# Revit family: JC KONTAKTER JCK119 Armbågskontakt
name_source: partatom
category: Specialty Equipment
units: mm (PartAtom-declared; Revit-internal decimal feet)

## family parameters
Always vertical = Yes
Cut with Voids When Loaded = No
Enable Cutting in Views = Yes
Host = Wall
Maintain Annotation Orientation = No
Part Type = Normal
Room Calculation Point = No
Round Connector Dimension = Use Diameter
Shared = No

## types (1)
- Armbågskontakt JCK119
    Antal mikrobrytare = 1
    CE Dokument = https://jckontakter.se
    Core Finish = Aluminum ENAW 6060 (guldeoxerad)
    Default Elevation = 0 mm  [stored 0 ft]
    Description = JCK119 är en tålig armbågskontakt med plan tryckplatta och endcap i mässing, samt underdel i guldeloxerad aluminium. Modellen är utvecklad för att användas i exklusiva miljöer och i äldre, k-märkta byggnader. JCK119 går bra att beställa med radiostyrning då det ofta är svårt att komma fram med kablage i äldre byggnader.
    End Cap Finish = Mässing
    Lid Finish = Mässing
    Längsta märkström = 1mA/4 V DC
    Manufacturer = JC Kontakter
    Microbrytare = Standard NO IP67
    Model = JCK119
    Nominell märkström = 12 V - Resistive 6A Inductive L/R 5ms 6A, 24 V - Resistive 6A Inductive L/R 5ms 5A
    Placering information = https://jckontakter.se
    Produktvikt = 0.579 kg
    Screw Finish = Mässing
    Teknisk produktblad = https://jckontakter.se
    Tillvalsförteckning = https://jckontakter.se
    Tillverkarens land = Sverige
    URL = https://jckontakter.se

note: [stored X ft] marks values corroborated as IEEE doubles in the binary element streams (Revit-internal decimal feet)

## geometry (parser evidence)
native form markers: Sweep x4
no freeform markers — native parametric forms only
